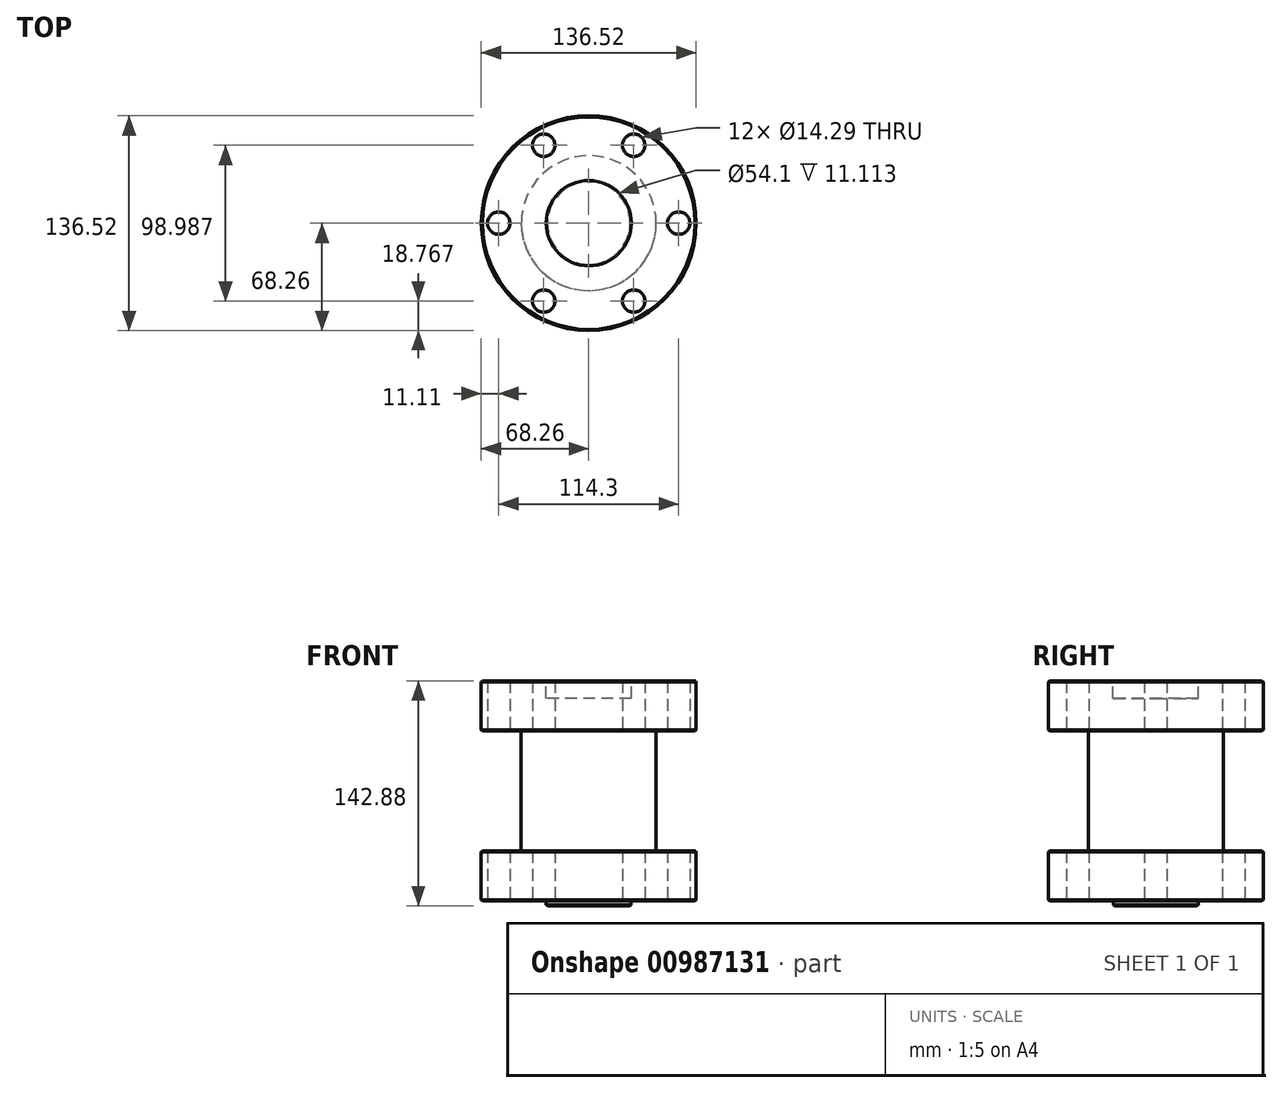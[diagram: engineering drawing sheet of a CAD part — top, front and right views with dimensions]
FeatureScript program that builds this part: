
annotation { "Feature Type Name" : "Feature", "Feature Type Description" : "" }
export const myFeature = defineFeature(function(context is Context, id is Id, definition is map)
    precondition{}
    {
        {
            var Q0;
            Q0=qCreatedBy(makeId("Top.planeOp"),FACE);
            var sketch = newSketch(context, id + "F0", { "sketchPlane" : qUnion([Q0])});
            skCircle(sketch, "E0", {"center": v(0, 0) * mm, "radius": 68.26 * mm});
            skCircle(sketch, "E1", {"center": v(0, 0) * mm, "radius": 57.15 * mm, "construction": true});
            skLineSegment(sketch, "E2", {"start": v(0, 0) * mm, "end": v(0, 107.05) * mm, "construction": true});
            skLineSegment(sketch, "E3", {"start": v(0, 0) * mm, "end": v(52.26, 90.52) * mm, "construction": true});
            skCircle(sketch, "E4", {"center": v(28.58, 49.5) * mm, "radius": 7.14 * mm});
            skCircle(sketch, "E5.1.0", {"center": v(-28.57, 49.5) * mm, "radius": 7.14 * mm});
            skCircle(sketch, "E5.2.0", {"center": v(-57.15, 0) * mm, "radius": 7.14 * mm});
            skCircle(sketch, "E5.3.0", {"center": v(-28.58, -49.5) * mm, "radius": 7.14 * mm});
            skCircle(sketch, "E5.4.0", {"center": v(28.57, -49.5) * mm, "radius": 7.14 * mm});
            skCircle(sketch, "E5.5.0", {"center": v(57.15, 0) * mm, "radius": 7.14 * mm});
            skSolve(sketch);
        }
        {
            var Q0;
            Q0 = qSketchRegion(id + "F0", true);
            extrude(context, id + "F1", {"entities" : qUnion([Q0]), "depth" : 31.75 * mm, "offsetDistance" : 25.4 * mm});
        }
        {
            var Q0;
            Q0=makeQuery(id+"F1.opExtrude","CAP_FACE",FACE,{"disambiguationData":[OSD([sQuery(id+"F0.wireOp",EDGE,"E0"),sQuery(id+"F0.wireOp",EDGE,"E4"),sQuery(id+"F0.wireOp",EDGE,"E5.1.0"),sQuery(id+"F0.wireOp",EDGE,"E5.2.0"),sQuery(id+"F0.wireOp",EDGE,"E5.3.0"),sQuery(id+"F0.wireOp",EDGE,"E5.4.0"),sQuery(id+"F0.wireOp",EDGE,"E5.5.0")])],"isStart":false});
            cPlane(context, id + "F2", {"entities" : qUnion([Q0]), "cplaneType" : CPlaneType.OFFSET, "offset" : 139.7 * mm, "oppositeDirection" : true, "width" : 152.4 * mm, "height" : 152.4 * mm});
        }
        {
            var Q0;
            Q0=qCreatedBy(id+"F2.planeOp",FACE);
            var sketch = newSketch(context, id + "F3", { "sketchPlane" : qUnion([Q0])});
            skCircle(sketch, "E6", {"center": v(0, 0) * mm, "radius": 68.26 * mm});
            skCircle(sketch, "E7", {"center": v(0, 0) * mm, "radius": 57.15 * mm, "construction": true});
            skLineSegment(sketch, "E8", {"start": v(0, 0) * mm, "end": v(4.55, -5.34) * mm, "construction": true});
            skLineSegment(sketch, "E9", {"start": v(0, 0) * mm, "end": v(52.78, -91.42) * mm, "construction": true});
            skLineSegment(sketch, "E10", {"start": v(0, 0) * mm, "end": v(0, -103.83) * mm, "construction": true});
            skCircle(sketch, "E11", {"center": v(28.58, -49.5) * mm, "radius": 7.14 * mm});
            skCircle(sketch, "E12.1.0", {"center": v(57.15, 0) * mm, "radius": 7.14 * mm});
            skCircle(sketch, "E12.2.0", {"center": v(28.57, 49.5) * mm, "radius": 7.14 * mm});
            skCircle(sketch, "E12.3.0", {"center": v(-28.58, 49.5) * mm, "radius": 7.14 * mm});
            skCircle(sketch, "E12.4.0", {"center": v(-57.15, 0) * mm, "radius": 7.14 * mm});
            skCircle(sketch, "E12.5.0", {"center": v(-28.57, -49.5) * mm, "radius": 7.14 * mm});
            skSolve(sketch);
        }
        {
            var Q0;
            Q0 = qSketchRegion(id + "F3", true);
            extrude(context, id + "F4", {"entities" : qUnion([Q0]), "depth" : 31.75 * mm, "offsetDistance" : 25.4 * mm});
        }
        {
            var Q0;
            Q0=makeQuery(id+"F1.opExtrude","CAP_FACE",FACE,{"disambiguationData":[OSD([sQuery(id+"F0.wireOp",EDGE,"E0"),sQuery(id+"F0.wireOp",EDGE,"E4"),sQuery(id+"F0.wireOp",EDGE,"E5.1.0"),sQuery(id+"F0.wireOp",EDGE,"E5.2.0"),sQuery(id+"F0.wireOp",EDGE,"E5.3.0"),sQuery(id+"F0.wireOp",EDGE,"E5.4.0"),sQuery(id+"F0.wireOp",EDGE,"E5.5.0")])],"isStart":true});
            var sketch = newSketch(context, id + "F5", { "sketchPlane" : qUnion([Q0])});
            skCircle(sketch, "E13", {"center": v(0, 0) * mm, "radius": 42.86 * mm});
            skSolve(sketch);
        }
        {
            var Q0;
            Q0 = qSketchRegion(id + "F5", true);
            extrude(context, id + "F6", {"entities" : qUnion([Q0]), "operationType" : NewBodyOperationType.ADD, "depth" : 81.28 * mm, "offsetDistance" : 25.4 * mm});
        }
        {
            var Q0;
            Q0=makeQuery(id+"F1.opExtrude","CAP_FACE",FACE,{"disambiguationData":[OSD([sQuery(id+"F0.wireOp",EDGE,"E0"),sQuery(id+"F0.wireOp",EDGE,"E4"),sQuery(id+"F0.wireOp",EDGE,"E5.1.0"),sQuery(id+"F0.wireOp",EDGE,"E5.2.0"),sQuery(id+"F0.wireOp",EDGE,"E5.3.0"),sQuery(id+"F0.wireOp",EDGE,"E5.4.0"),sQuery(id+"F0.wireOp",EDGE,"E5.5.0")])],"isStart":false});
            var sketch = newSketch(context, id + "F7", { "sketchPlane" : qUnion([Q0])});
            skCircle(sketch, "E14", {"center": v(0, 0) * mm, "radius": 27.05 * mm});
            skSolve(sketch);
        }
        {
            var Q0;
            Q0 = qSketchRegion(id + "F7", true);
            extrude(context, id + "F8", {"entities" : qUnion([Q0]), "operationType" : NewBodyOperationType.REMOVE, "oppositeDirection" : true, "depth" : 11.1 * mm, "offsetDistance" : 25.4 * mm});
        }
        {
            var Q0;
            Q0=makeQuery(id+"F4.opExtrude","CAP_FACE",FACE,{"disambiguationData":[OSD([sQuery(id+"F3.wireOp",EDGE,"E6"),sQuery(id+"F3.wireOp",EDGE,"E11"),sQuery(id+"F3.wireOp",EDGE,"E12.1.0"),sQuery(id+"F3.wireOp",EDGE,"E12.2.0"),sQuery(id+"F3.wireOp",EDGE,"E12.3.0"),sQuery(id+"F3.wireOp",EDGE,"E12.4.0"),sQuery(id+"F3.wireOp",EDGE,"E12.5.0")])],"isStart":true});
            var sketch = newSketch(context, id + "F9", { "sketchPlane" : qUnion([Q0])});
            skCircle(sketch, "E15", {"center": v(0, 0) * mm, "radius": 26.99 * mm});
            skSolve(sketch);
        }
        {
            var Q0;
            Q0 = qSketchRegion(id + "F9", true);
            extrude(context, id + "F10", {"entities" : qUnion([Q0]), "operationType" : NewBodyOperationType.ADD, "depth" : 3.17 * mm, "offsetDistance" : 25.4 * mm});
        }
        {
            var Q0;
            Q0=makeQuery(id+"F1.opExtrude","CAP_EDGE",EDGE,{"disambiguationData":[OSD([sQuery(id+"F0.wireOp",EDGE,"E0")])],"isStart":false});
            var Q1;
            Q1=makeQuery(id+"F8.boolean.opBoolean","COPY",EDGE,{"derivedFrom":makeQuery(id+"F8.opExtrude","CAP_EDGE",EDGE,{"disambiguationData":[OSD([sQuery(id+"F7.wireOp",EDGE,"E14")])],"isStart":true})});
            var Q2;
            Q2=makeQuery(id+"F1.opExtrude","CAP_EDGE",EDGE,{"disambiguationData":[OSD([sQuery(id+"F0.wireOp",EDGE,"E0")])],"isStart":true});
            var Q3;
            Q3=makeQuery(id+"F4.opExtrude","CAP_EDGE",EDGE,{"disambiguationData":[OSD([sQuery(id+"F3.wireOp",EDGE,"E6")])],"isStart":false});
            var Q4;
            Q4=makeQuery(id+"F4.opExtrude","CAP_EDGE",EDGE,{"disambiguationData":[OSD([sQuery(id+"F3.wireOp",EDGE,"E6")])],"isStart":true});
            var Q5;
            Q5=makeQuery(id+"F10.opExtrude","CAP_EDGE",EDGE,{"disambiguationData":[OSD([sQuery(id+"F9.wireOp",EDGE,"E15")])],"isStart":false});
            chamfer(context, id + "F11", {"entities" : qUnion([Q0, Q1, Q2, Q3, Q4, Q5]), "width" : 0.76 * mm, "tangentPropagation" : true});
        }
    });
